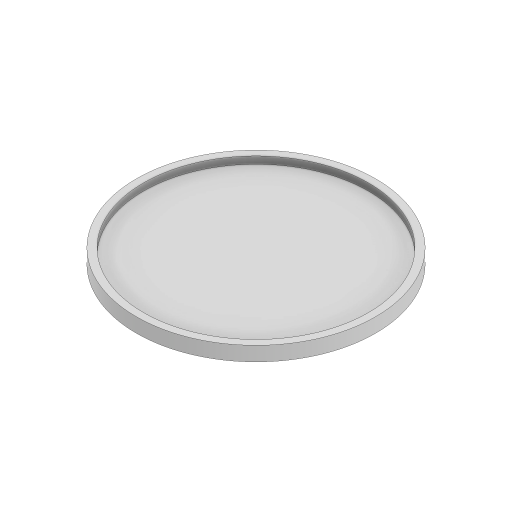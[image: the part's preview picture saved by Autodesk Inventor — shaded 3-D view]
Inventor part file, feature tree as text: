
AUTODESK INVENTOR PART (.ipt)
format: ipt  version: 2023 (Build 270158000, 158)  size: 106,496 bytes
history: native  units: in
note: dims shown in document units (in); Inventor stores cm internally (conversion verified against a paired STEP export)
features: extrude x2, sketch x2, projected_geometry x1
ambient origin geometry x8: Origin, YZ Plane, XZ Plane, XY Plane, X Axis, Y Axis, Z Axis, Center Point
bodies: Solid1 (feature_tree)
feature tree (5):
  extrude  "Extrusion1"  Depth=236.2205in TaperAngle=0.0deg
  extrude  "Extrusion2"  [1 undecoded]
  sketch  "Sketch1"  dims[d0=3937.0079in d1=236.2205in d2=0.0in]
  sketch  "Sketch2"  dims[d3=118.1102in d4=0.0in]
  projected_geometry  "Projected Loop1"
note: 1 required parameter value undecoded (feature->parameter linkage not recoverable at this tier; creation-order binding heuristic only, values carry confidence <= 0.55)
